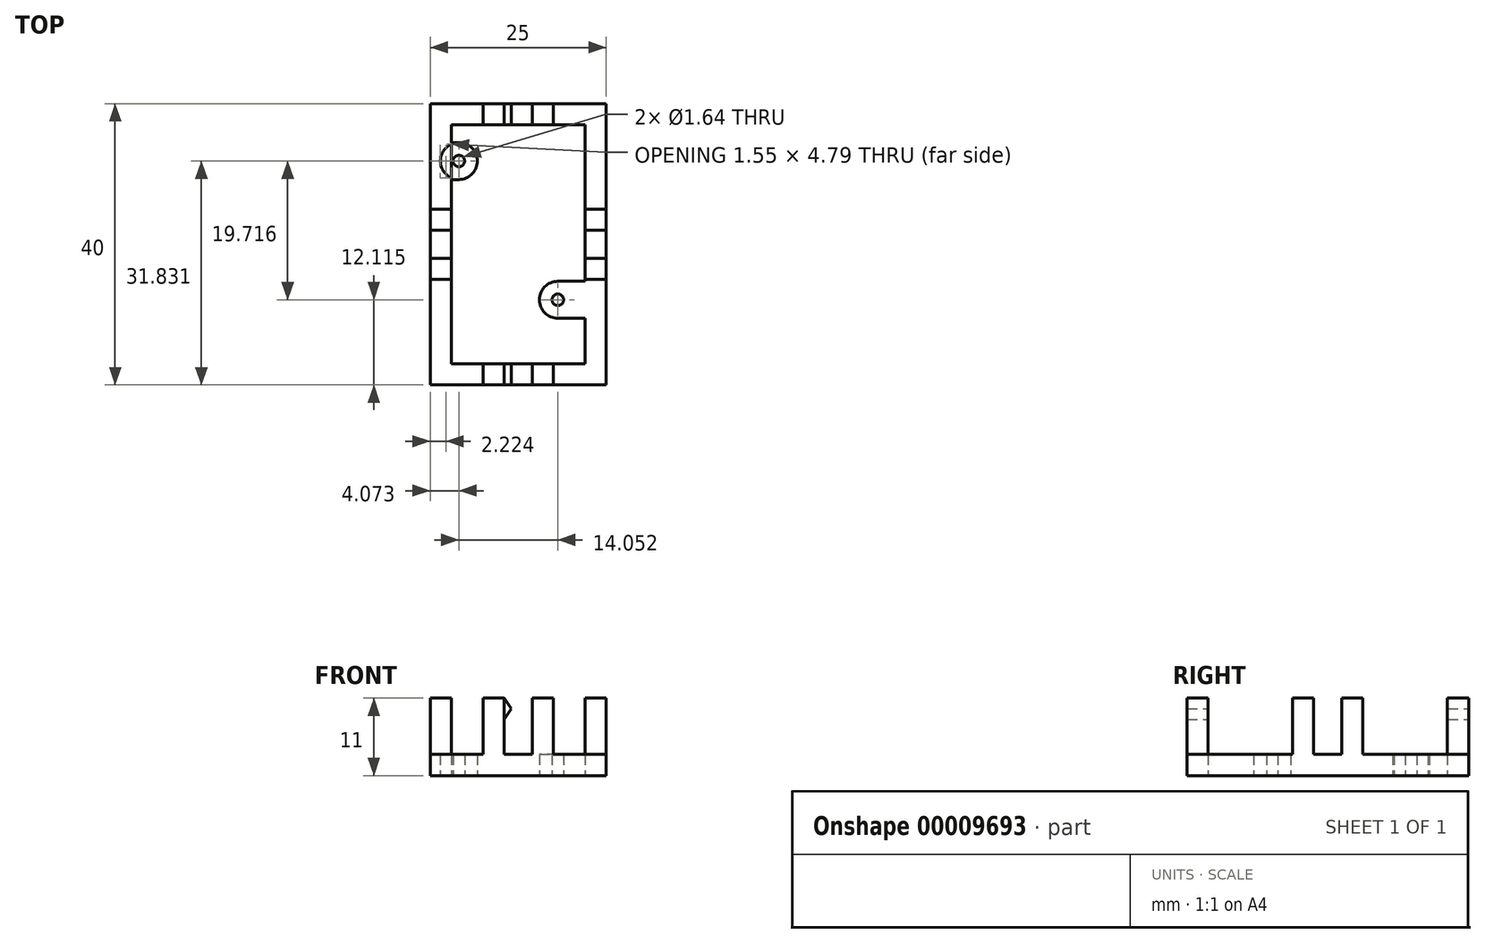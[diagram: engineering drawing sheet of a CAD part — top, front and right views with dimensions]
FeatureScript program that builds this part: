
annotation { "Feature Type Name" : "Feature", "Feature Type Description" : "" }
export const myFeature = defineFeature(function(context is Context, id is Id, definition is map)
    precondition{}
    {
        {
            var Q0;
            Q0=qCreatedBy(makeId("Top.planeOp"),FACE);
            var sketch = newSketch(context, id + "F0", { "sketchPlane" : qUnion([Q0])});
            skLineSegment(sketch, "E0.bottom", {"start": v(-9.5, 17) * mm, "end": v(9.5, 17) * mm});
            skLineSegment(sketch, "E0.top", {"start": v(-9.5, -17) * mm, "end": v(9.5, -17) * mm});
            skLineSegment(sketch, "E0.left", {"start": v(-9.5, 17) * mm, "end": v(-9.5, -17) * mm});
            skLineSegment(sketch, "E0.right", {"start": v(9.5, 17) * mm, "end": v(9.5, -17) * mm});
            skLineSegment(sketch, "E1.bottom", {"start": v(-12.5, 20) * mm, "end": v(12.5, 20) * mm});
            skLineSegment(sketch, "E1.top", {"start": v(-12.5, -20) * mm, "end": v(12.5, -20) * mm});
            skLineSegment(sketch, "E1.left", {"start": v(-12.5, 20) * mm, "end": v(-12.5, -20) * mm});
            skLineSegment(sketch, "E1.right", {"start": v(12.5, 20) * mm, "end": v(12.5, -20) * mm});
            skCircle(sketch, "E2", {"center": v(-8.43, 11.83) * mm, "radius": 2.62 * mm});
            skCircle(sketch, "E3", {"center": v(-8.43, 11.83) * mm, "radius": 0.82 * mm});
            skLineSegment(sketch, "E4", {"start": v(-8.43, 14.46) * mm, "end": v(-9.5, 14.46) * mm});
            skLineSegment(sketch, "E5", {"start": v(-8.43, 9.2) * mm, "end": v(-9.5, 9.2) * mm});
            skCircle(sketch, "E6", {"center": v(5.62, -7.89) * mm, "radius": 2.62 * mm});
            skCircle(sketch, "E7", {"center": v(5.62, -7.89) * mm, "radius": 0.82 * mm});
            skLineSegment(sketch, "E8", {"start": v(5.62, -5.26) * mm, "end": v(9.5, -5.26) * mm});
            skLineSegment(sketch, "E9", {"start": v(5.62, -10.5) * mm, "end": v(9.5, -10.5) * mm});
            skSolve(sketch);
        }
        {
            var Q0;
            {var subQ3=sQuery(id+"F0.wireOp",EDGE,"E4");Q0=makeQuery(id+"F0.imprint","IMPRINT",FACE,{"disambiguationData":[TD([[makeQuery(id+"F0.imprint","IMPRINT",EDGE,{"derivedFrom":subQ3}),1.0]])]});}
            var Q1;
            Q1=makeQuery(id+"F0.imprint","IMPRINT",FACE,{"disambiguationData":[TD([[makeQuery(id+"F0.imprint","IMPRINT",EDGE,{"derivedFrom":sQuery(id+"F0.wireOp",EDGE,"E3")}),-1.0]])]});
            var Q2;
            {var subQ0=sQuery(id+"F0.wireOp",EDGE,"E2");var subQ1=sQuery(id+"F0.wireOp",EDGE,"E0.left");var subQ3=makeQuery(id+"F0.imprint","INTERSECT",VERTEX,{"disambiguationData":[OD(0.0)],"derivedFrom":[subQ1,subQ0]});Q2=makeQuery(id+"F0.imprint","IMPRINT",FACE,{"disambiguationData":[TD([[makeQuery(id+"F0.imprint","IMPRINT",EDGE,{"disambiguationData":[TD([[subQ3,-1.0]])],"derivedFrom":subQ1}),-1.0]])]});}
            var Q3;
            {var subQ10=sQuery(id+"F0.wireOp",EDGE,"E0.bottom");Q3=makeQuery(id+"F0.imprint","IMPRINT",FACE,{"disambiguationData":[TD([[makeQuery(id+"F0.imprint","IMPRINT",EDGE,{"derivedFrom":subQ10}),1.0]])]});}
            var Q4;
            {var subQ0=sQuery(id+"F0.wireOp",EDGE,"E5");Q4=makeQuery(id+"F0.imprint","IMPRINT",FACE,{"disambiguationData":[TD([[makeQuery(id+"F0.imprint","IMPRINT",EDGE,{"derivedFrom":subQ0}),-1.0]])]});}
            var Q5;
            {var subQ1=sQuery(id+"F0.wireOp",EDGE,"E8");Q5=makeQuery(id+"F0.imprint","IMPRINT",FACE,{"disambiguationData":[TD([[makeQuery(id+"F0.imprint","IMPRINT",EDGE,{"derivedFrom":subQ1}),-1.0]])]});}
            var Q6;
            Q6=makeQuery(id+"F0.imprint","IMPRINT",FACE,{"disambiguationData":[TD([[makeQuery(id+"F0.imprint","IMPRINT",EDGE,{"derivedFrom":sQuery(id+"F0.wireOp",EDGE,"E7")}),-1.0]])]});
            extrude(context, id + "F1", {"entities" : qUnion([Q0, Q1, Q2, Q3, Q4, Q5, Q6]), "depth" : 3 * mm});
        }
        {
            var Q0;
            Q0=qCreatedBy(makeId("Top.planeOp"),FACE);
            var sketch = newSketch(context, id + "F2", { "sketchPlane" : qUnion([Q0])});
            skLineSegment(sketch, "E10.bottom", {"start": v(-12.5, 5) * mm, "end": v(-9.5, 5) * mm});
            skLineSegment(sketch, "E10.top", {"start": v(-12.5, 2) * mm, "end": v(-9.5, 2) * mm});
            skLineSegment(sketch, "E10.left", {"start": v(-12.5, 5) * mm, "end": v(-12.5, 2) * mm});
            skLineSegment(sketch, "E10.right", {"start": v(-9.5, 5) * mm, "end": v(-9.5, 2) * mm});
            skLineSegment(sketch, "E11.bottom", {"start": v(9.5, 5) * mm, "end": v(12.5, 5) * mm});
            skLineSegment(sketch, "E11.top", {"start": v(9.5, 2) * mm, "end": v(12.5, 2) * mm});
            skLineSegment(sketch, "E11.left", {"start": v(9.5, 5) * mm, "end": v(9.5, 2) * mm});
            skLineSegment(sketch, "E11.right", {"start": v(12.5, 5) * mm, "end": v(12.5, 2) * mm});
            skLineSegment(sketch, "E12.bottom", {"start": v(-12.5, -2) * mm, "end": v(-9.5, -2) * mm});
            skLineSegment(sketch, "E12.top", {"start": v(-12.5, -5) * mm, "end": v(-9.5, -5) * mm});
            skLineSegment(sketch, "E12.left", {"start": v(-12.5, -2) * mm, "end": v(-12.5, -5) * mm});
            skLineSegment(sketch, "E12.right", {"start": v(-9.5, -2) * mm, "end": v(-9.5, -5) * mm});
            skLineSegment(sketch, "E13.bottom", {"start": v(9.5, -2) * mm, "end": v(12.5, -2) * mm});
            skLineSegment(sketch, "E13.top", {"start": v(9.5, -5) * mm, "end": v(12.5, -5) * mm});
            skLineSegment(sketch, "E13.left", {"start": v(9.5, -2) * mm, "end": v(9.5, -5) * mm});
            skLineSegment(sketch, "E13.right", {"start": v(12.5, -2) * mm, "end": v(12.5, -5) * mm});
            skLineSegment(sketch, "E14.bottom", {"start": v(-5, 20) * mm, "end": v(-2, 20) * mm});
            skLineSegment(sketch, "E14.top", {"start": v(-5, 17) * mm, "end": v(-2, 17) * mm});
            skLineSegment(sketch, "E14.left", {"start": v(-5, 20) * mm, "end": v(-5, 17) * mm});
            skLineSegment(sketch, "E14.right", {"start": v(-2, 20) * mm, "end": v(-2, 17) * mm});
            skLineSegment(sketch, "E15.top", {"start": v(2, 17) * mm, "end": v(5, 17) * mm});
            skLineSegment(sketch, "E15.left", {"start": v(2, 20) * mm, "end": v(2, 17) * mm});
            skLineSegment(sketch, "E15.bottom", {"start": v(2, 20) * mm, "end": v(5, 20) * mm});
            skLineSegment(sketch, "E15.right", {"start": v(5, 20) * mm, "end": v(5, 17) * mm});
            skLineSegment(sketch, "E16.bottom", {"start": v(-5, -17) * mm, "end": v(-2, -17) * mm});
            skLineSegment(sketch, "E17.right", {"start": v(5, -17) * mm, "end": v(5, -20) * mm});
            skLineSegment(sketch, "E16.top", {"start": v(-5, -20) * mm, "end": v(-2, -20) * mm});
            skLineSegment(sketch, "E17.bottom", {"start": v(2, -17) * mm, "end": v(5, -17) * mm});
            skLineSegment(sketch, "E17.left", {"start": v(2, -17) * mm, "end": v(2, -20) * mm});
            skLineSegment(sketch, "E17.top", {"start": v(2, -20) * mm, "end": v(5, -20) * mm});
            skLineSegment(sketch, "E16.right", {"start": v(-2, -17) * mm, "end": v(-2, -20) * mm});
            skLineSegment(sketch, "E16.left", {"start": v(-5, -17) * mm, "end": v(-5, -20) * mm});
            skSolve(sketch);
        }
        {
            var Q0;
            Q0 = qSketchRegion(id + "F2", true);
            extrude(context, id + "F3", {"entities" : qUnion([Q0]), "operationType" : NewBodyOperationType.ADD, "depth" : 11 * mm});
        }
        {
            var Q0;
            Q0=makeQuery(id+"F3.boolean.opBoolean","MERGE",FACE,{"derivedFrom":[makeQuery(id+"F1.opExtrude","SWEPT_FACE",FACE,{"disambiguationData":[OSD([sQuery(id+"F0.wireOp",EDGE,"E1.bottom")])]}),makeQuery(id+"F3.opExtrude","SWEPT_FACE",FACE,{"disambiguationData":[OSD([sQuery(id+"F2.wireOp",EDGE,"E14.bottom")])]}),makeQuery(id+"F3.opExtrude","SWEPT_FACE",FACE,{"disambiguationData":[OSD([sQuery(id+"F2.wireOp",EDGE,"E15.bottom")])]})]});
            var sketch = newSketch(context, id + "F4", { "sketchPlane" : qUnion([Q0])});
            skLineSegment(sketch, "E18", {"start": v(2, 11) * mm, "end": v(1, 9.5) * mm});
            skLineSegment(sketch, "E19", {"start": v(1, 9.5) * mm, "end": v(2, 8) * mm});
            skSolve(sketch);
        }
        {
            var Q0;
            {var subQ3=sQuery(id+"F4.wireOp",EDGE,"E18");Q0=makeQuery(id+"F4.imprint","IMPRINT",FACE,{"disambiguationData":[TD([[makeQuery(id+"F4.imprint","IMPRINT",EDGE,{"derivedFrom":subQ3}),1.0]])]});}
            extrude(context, id + "F5", {"entities" : qUnion([Q0]), "oppositeDirection" : true, "depth" : 3 * mm});
        }
        {
            var Q0;
            Q0=makeQuery(id+"F3.boolean.opBoolean","MERGE",FACE,{"derivedFrom":[makeQuery(id+"F1.opExtrude","SWEPT_FACE",FACE,{"disambiguationData":[OSD([sQuery(id+"F0.wireOp",EDGE,"E0.top")])]}),makeQuery(id+"F3.opExtrude","SWEPT_FACE",FACE,{"disambiguationData":[OSD([sQuery(id+"F2.wireOp",EDGE,"E16.bottom")])]}),makeQuery(id+"F3.opExtrude","SWEPT_FACE",FACE,{"disambiguationData":[OSD([sQuery(id+"F2.wireOp",EDGE,"E17.bottom")])]})]});
            var sketch = newSketch(context, id + "F6", { "sketchPlane" : qUnion([Q0])});
            skLineSegment(sketch, "E20", {"start": v(2, 11) * mm, "end": v(1, 9.5) * mm});
            skLineSegment(sketch, "E21", {"start": v(1, 9.5) * mm, "end": v(2, 8) * mm});
            skSolve(sketch);
        }
        {
            var Q0;
            {var subQ3=sQuery(id+"F6.wireOp",EDGE,"E20");Q0=makeQuery(id+"F6.imprint","IMPRINT",FACE,{"disambiguationData":[TD([[makeQuery(id+"F6.imprint","IMPRINT",EDGE,{"derivedFrom":subQ3}),1.0]])]});}
            extrude(context, id + "F7", {"entities" : qUnion([Q0]), "oppositeDirection" : true, "depth" : 3 * mm});
        }
    });
